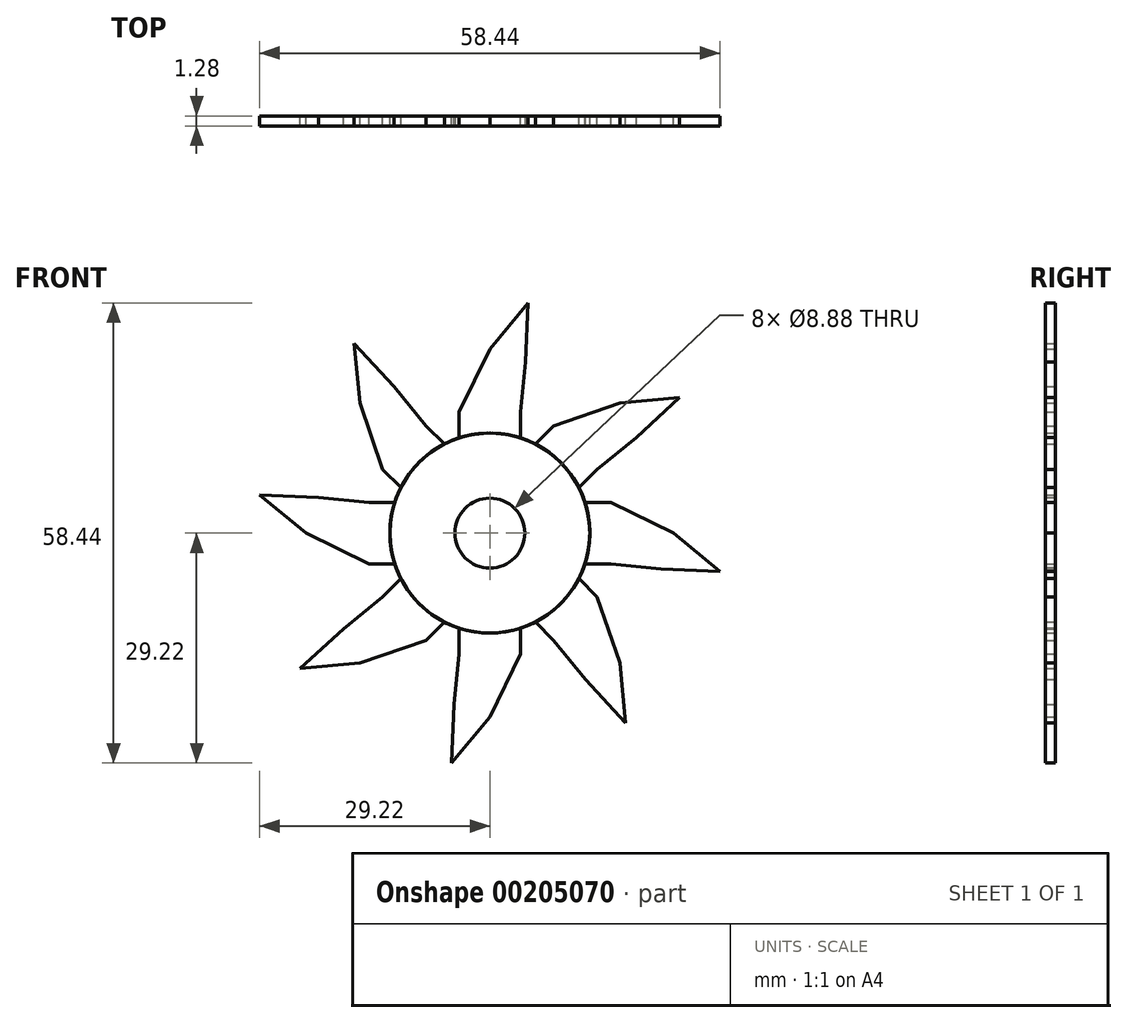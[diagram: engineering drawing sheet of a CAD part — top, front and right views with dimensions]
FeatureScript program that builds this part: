
annotation { "Feature Type Name" : "Feature", "Feature Type Description" : "" }
export const myFeature = defineFeature(function(context is Context, id is Id, definition is map)
    precondition{}
    {
        {
            var Q0;
            Q0=qCreatedBy(makeId("Front.planeOp"),FACE);
            var sketch = newSketch(context, id + "F0", { "sketchPlane" : qUnion([Q0])});
            skCircle(sketch, "E0", {"center": v(0, 0) * mm, "radius": 12.7 * mm});
            skSolve(sketch);
        }
        {
            var Q0;
            Q0=qSketchRegion(id+"F0",true);
            extrude(context, id + "F1", {"entities" : qUnion([Q0]), "endBound" : BoundingType.SYMMETRIC, "depth" : 1.27 * mm});
        }
        {
            var Q0;
            Q0=qCreatedBy(makeId("Front.planeOp"),FACE);
            var sketch = newSketch(context, id + "F2", { "sketchPlane" : qUnion([Q0])});
            skLineSegment(sketch, "E1.bottom", {"start": v(3.9, 15.36) * mm, "end": v(-3.9, 15.36) * mm});
            skLineSegment(sketch, "E1.top", {"start": v(3.9, 9.4) * mm, "end": v(-3.9, 9.4) * mm});
            skLineSegment(sketch, "E1.left", {"start": v(3.9, 15.36) * mm, "end": v(3.9, 9.4) * mm});
            skLineSegment(sketch, "E1.right", {"start": v(-3.9, 15.36) * mm, "end": v(-3.9, 9.4) * mm});
            skPoint(sketch, "E1.middle", {"position": v(0, 12.38) * mm});
            skLineSegment(sketch, "E2", {"start": v(-3.9, 15.36) * mm, "end": v(0, 23.36) * mm});
            skLineSegment(sketch, "E3", {"start": v(0, 23.36) * mm, "end": v(4.55, 21.76) * mm});
            skLineSegment(sketch, "E4", {"start": v(4.55, 21.76) * mm, "end": v(3.9, 15.36) * mm});
            skLineSegment(sketch, "E5", {"start": v(0, 23.36) * mm, "end": v(4.86, 29.22) * mm});
            skLineSegment(sketch, "E6", {"start": v(4.86, 29.22) * mm, "end": v(4.55, 21.76) * mm});
            skSolve(sketch);
        }
        {
            var Q0;
            Q0=qSketchRegion(id+"F2",true);
            extrude(context, id + "F3", {"entities" : qUnion([Q0]), "operationType" : NewBodyOperationType.ADD, "endBound" : BoundingType.SYMMETRIC, "depth" : 1.27 * mm});
        }
        {
            var Q0;
            Q0=makeQuery(id+"F1.opExtrude","SWEPT_BODY",BODY,{"disambiguationData":[OSD([sQuery(id+"F0.wireOp",EDGE,"E0")])]});
            var Q1;
            Q1=sQuery(id+"F0.wireOp",EDGE,"E0");
            circularPattern(context, id + "F4", {"entities" : qUnion([Q0]), "axis" : qUnion([Q1]), "angle" : 360 * degree, "instanceCount" : 8, "equalSpace" : true});
        }
        {
            var Q0;
            Q0=qCreatedBy(makeId("Front.planeOp"),FACE);
            var sketch = newSketch(context, id + "F5", { "sketchPlane" : qUnion([Q0])});
            skCircle(sketch, "E7", {"center": v(0, 0) * mm, "radius": 4.44 * mm});
            skSolve(sketch);
        }
        {
            var Q0;
            Q0=qSketchRegion(id+"F5",true);
            extrude(context, id + "F6", {"entities" : qUnion([Q0]), "operationType" : NewBodyOperationType.REMOVE, "endBound" : BoundingType.SYMMETRIC, "oppositeDirection" : true, "depth" : 1.27 * mm});
        }
    });
